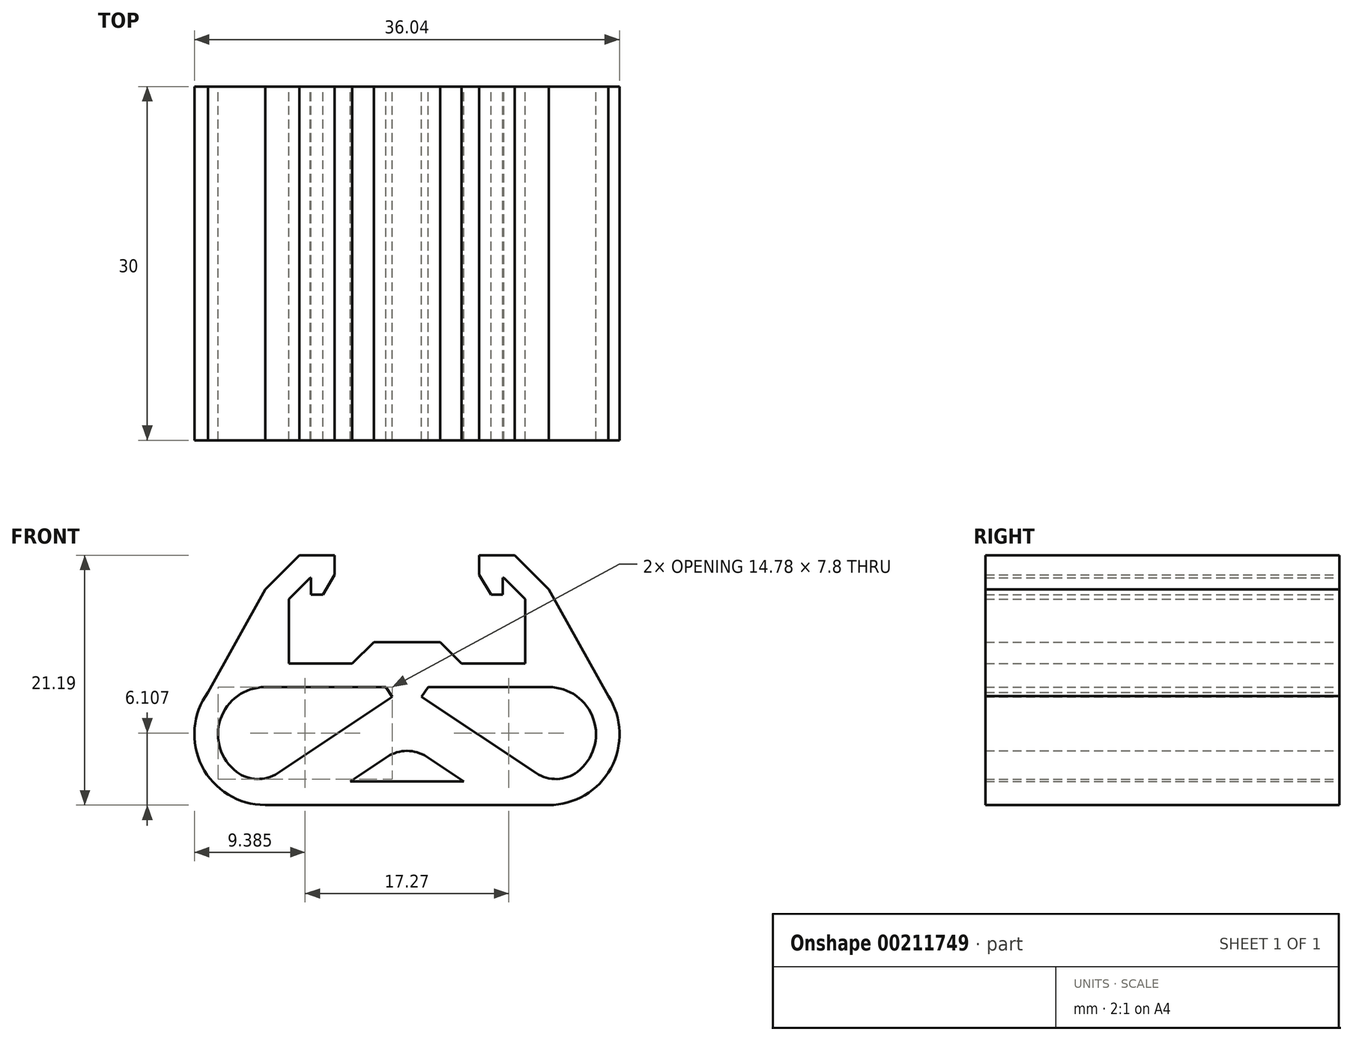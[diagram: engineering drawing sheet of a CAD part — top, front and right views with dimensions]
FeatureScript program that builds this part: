
annotation { "Feature Type Name" : "Feature", "Feature Type Description" : "" }
export const myFeature = defineFeature(function(context is Context, id is Id, definition is map)
    precondition{}
    {
        {
            var Q0;
            Q0=qCreatedBy(makeId("Front.planeOp"),FACE);
            var sketch = newSketch(context, id + "F0", { "sketchPlane" : qUnion([Q0])});
            skLineSegment(sketch, "E0", {"start": v(2.84, -8.2) * mm, "end": v(5.5, -8.2) * mm, "construction": true});
            skLineSegment(sketch, "E1", {"start": v(5.5, -8.2) * mm, "end": v(5.5, -6.56) * mm, "construction": true});
            skLineSegment(sketch, "E2", {"start": v(5.5, -6.56) * mm, "end": v(2.84, -3.9) * mm, "construction": true});
            skLineSegment(sketch, "E3", {"start": v(2.84, -3.9) * mm, "end": v(-2.84, -3.9) * mm, "construction": true});
            skLineSegment(sketch, "E4", {"start": v(-2.84, -3.9) * mm, "end": v(-5.5, -6.56) * mm, "construction": true});
            skLineSegment(sketch, "E5", {"start": v(-5.5, -6.56) * mm, "end": v(-5.5, -8.2) * mm, "construction": true});
            skLineSegment(sketch, "E6", {"start": v(-5.5, -8.2) * mm, "end": v(-2.84, -8.2) * mm, "construction": true});
            skLineSegment(sketch, "E7", {"start": v(-4.64, -10) * mm, "end": v(-10, -10) * mm, "construction": true});
            skLineSegment(sketch, "E8", {"start": v(-10, -10) * mm, "end": v(-10, -4.64) * mm, "construction": true});
            skLineSegment(sketch, "E9", {"start": v(-10, -4.64) * mm, "end": v(-8.2, -2.84) * mm, "construction": true});
            skLineSegment(sketch, "E10", {"start": v(-8.2, -2.84) * mm, "end": v(-8.2, -5.5) * mm, "construction": true});
            skLineSegment(sketch, "E11", {"start": v(-8.2, -5.5) * mm, "end": v(-6.56, -5.5) * mm, "construction": true});
            skLineSegment(sketch, "E12", {"start": v(-6.56, -5.5) * mm, "end": v(-3.9, -2.84) * mm, "construction": true});
            skLineSegment(sketch, "E13", {"start": v(-3.9, -2.84) * mm, "end": v(-3.9, 2.84) * mm, "construction": true});
            skLineSegment(sketch, "E14", {"start": v(-3.9, 2.84) * mm, "end": v(-6.56, 5.5) * mm, "construction": true});
            skLineSegment(sketch, "E15", {"start": v(-6.56, 5.5) * mm, "end": v(-8.2, 5.5) * mm, "construction": true});
            skLineSegment(sketch, "E16", {"start": v(-8.2, 5.5) * mm, "end": v(-8.2, 2.84) * mm, "construction": true});
            skLineSegment(sketch, "E17", {"start": v(-8.2, 2.84) * mm, "end": v(-10, 4.64) * mm, "construction": true});
            skLineSegment(sketch, "E18", {"start": v(-10, 4.64) * mm, "end": v(-10, 10) * mm, "construction": true});
            skLineSegment(sketch, "E19", {"start": v(-10, 10) * mm, "end": v(-4.64, 10) * mm, "construction": true});
            skLineSegment(sketch, "E20", {"start": v(-4.64, 10) * mm, "end": v(-2.84, 8.2) * mm, "construction": true});
            skLineSegment(sketch, "E21", {"start": v(-2.84, 8.2) * mm, "end": v(-5.5, 8.2) * mm, "construction": true});
            skLineSegment(sketch, "E22", {"start": v(-5.5, 8.2) * mm, "end": v(-5.5, 6.56) * mm, "construction": true});
            skLineSegment(sketch, "E23", {"start": v(-5.5, 6.56) * mm, "end": v(-2.84, 3.9) * mm, "construction": true});
            skLineSegment(sketch, "E24", {"start": v(-2.84, 3.9) * mm, "end": v(2.84, 3.9) * mm, "construction": true});
            skLineSegment(sketch, "E25", {"start": v(2.84, 3.9) * mm, "end": v(5.5, 6.56) * mm, "construction": true});
            skLineSegment(sketch, "E26", {"start": v(5.5, 6.56) * mm, "end": v(5.5, 8.2) * mm, "construction": true});
            skLineSegment(sketch, "E27", {"start": v(5.5, 8.2) * mm, "end": v(2.84, 8.2) * mm, "construction": true});
            skLineSegment(sketch, "E28", {"start": v(2.84, 8.2) * mm, "end": v(4.64, 10) * mm, "construction": true});
            skLineSegment(sketch, "E29", {"start": v(4.64, 10) * mm, "end": v(10, 10) * mm, "construction": true});
            skLineSegment(sketch, "E30", {"start": v(10, 10) * mm, "end": v(10, 4.64) * mm, "construction": true});
            skLineSegment(sketch, "E31", {"start": v(10, 4.64) * mm, "end": v(8.2, 2.84) * mm, "construction": true});
            skLineSegment(sketch, "E32", {"start": v(8.2, 2.84) * mm, "end": v(8.2, 5.5) * mm, "construction": true});
            skLineSegment(sketch, "E33", {"start": v(8.2, 5.5) * mm, "end": v(6.56, 5.5) * mm, "construction": true});
            skLineSegment(sketch, "E34", {"start": v(6.56, 5.5) * mm, "end": v(3.9, 2.84) * mm, "construction": true});
            skLineSegment(sketch, "E35", {"start": v(3.9, 2.84) * mm, "end": v(3.9, -2.84) * mm, "construction": true});
            skLineSegment(sketch, "E36", {"start": v(3.9, -2.84) * mm, "end": v(6.56, -5.5) * mm, "construction": true});
            skLineSegment(sketch, "E37", {"start": v(6.56, -5.5) * mm, "end": v(8.2, -5.5) * mm, "construction": true});
            skLineSegment(sketch, "E38", {"start": v(8.2, -5.5) * mm, "end": v(8.2, -2.84) * mm, "construction": true});
            skLineSegment(sketch, "E39", {"start": v(8.2, -2.84) * mm, "end": v(10, -4.64) * mm, "construction": true});
            skLineSegment(sketch, "E40", {"start": v(10, -4.64) * mm, "end": v(10, -10) * mm, "construction": true});
            skLineSegment(sketch, "E41", {"start": v(10, -10) * mm, "end": v(4.64, -10) * mm, "construction": true});
            skLineSegment(sketch, "E42.0", {"start": v(-10.03, -4.56) * mm, "end": v(-10.03, -10.02) * mm});
            skPoint(sketch, "E43.endSnap0", {"position": v(3.9, 0) * mm});
            skLineSegment(sketch, "E44", {"start": v(0, 0) * mm, "end": v(12.85, 0) * mm});
            skLineSegment(sketch, "E45.0", {"start": v(-10.02, -10.03) * mm, "end": v(-4.64, -10.03) * mm});
            skLineSegment(sketch, "E46.0", {"start": v(-6.13, -0.84) * mm, "end": v(-6.13, -2.5) * mm});
            skLineSegment(sketch, "E47", {"start": v(-8.12, -4.17) * mm, "end": v(-7.12, -4.17) * mm});
            skLineSegment(sketch, "E48.trimOffspring", {"start": v(-8.12, -10) * mm, "end": v(-8.12, -10.02) * mm});
            skLineSegment(sketch, "E49.0", {"start": v(-6.13, -0.84) * mm, "end": v(-9.13, -0.84) * mm});
            skLineSegment(sketch, "E50.trimOffspring", {"start": v(-8.12, -2.74) * mm, "end": v(-8.12, -4.17) * mm});
            skPoint(sketch, "E51.orphan", {"position": v(-8.2, -4.17) * mm});
            skLineSegment(sketch, "E52.0", {"start": v(-8.12, -2.74) * mm, "end": v(-8.2, -2.74) * mm});
            skLineSegment(sketch, "E53.0", {"start": v(-12.03, -12.03) * mm, "end": v(-1.8, -12.03) * mm});
            skLineSegment(sketch, "E54", {"start": v(-10.03, -4.56) * mm, "end": v(-8.2, -2.74) * mm});
            skLineSegment(sketch, "E55.0", {"start": v(-12.03, -3.74) * mm, "end": v(-9.13, -0.84) * mm});
            skLineSegment(sketch, "E56", {"start": v(-7.12, -4.17) * mm, "end": v(-6.13, -2.5) * mm});
            skLineSegment(sketch, "E57.MirrorCS", {"start": v(10.03, -4.56) * mm, "end": v(10.03, -10.02) * mm});
            skLineSegment(sketch, "E58.MirrorCS", {"start": v(10.03, -4.56) * mm, "end": v(8.2, -2.74) * mm});
            skLineSegment(sketch, "E59.MirrorCS", {"start": v(8.12, -2.74) * mm, "end": v(8.2, -2.74) * mm});
            skLineSegment(sketch, "E60.MirrorCS", {"start": v(8.12, -2.74) * mm, "end": v(8.12, -4.17) * mm});
            skLineSegment(sketch, "E61.MirrorCS", {"start": v(8.12, -4.17) * mm, "end": v(7.12, -4.17) * mm});
            skLineSegment(sketch, "E62.MirrorCS", {"start": v(7.12, -4.17) * mm, "end": v(6.12, -2.5) * mm});
            skLineSegment(sketch, "E63.MirrorCS", {"start": v(6.13, -0.84) * mm, "end": v(6.13, -2.5) * mm});
            skLineSegment(sketch, "E64.MirrorCS", {"start": v(6.13, -0.84) * mm, "end": v(9.13, -0.84) * mm});
            skLineSegment(sketch, "E65.MirrorCS", {"start": v(12.03, -3.74) * mm, "end": v(9.13, -0.84) * mm});
            skArc(sketch, "E66", {"start": v(12.03, -22.02) * mm, "mid": v(17.3, -18.9) * mm, "end": v(17.07, -12.78) * mm});
            skArc(sketch, "E67.MirrorC", {"start": v(-12.03, -22.02) * mm, "mid": v(-17.38, -18.73) * mm, "end": v(-16.85, -12.46) * mm});
            skArc(sketch, "E68.0", {"start": v(-14.44, -19.22) * mm, "mid": v(-15.82, -14.75) * mm, "end": v(-12.03, -12.02) * mm});
            skArc(sketch, "E69.0", {"start": v(14.44, -19.22) * mm, "mid": v(15.82, -14.75) * mm, "end": v(12.03, -12.02) * mm});
            skLineSegment(sketch, "E70.0", {"start": v(-12.03, -22.03) * mm, "end": v(12.03, -22.03) * mm});
            skLineSegment(sketch, "E71.0", {"start": v(-4.8, -20.03) * mm, "end": v(4.8, -20.03) * mm});
            skPoint(sketch, "E72.orphan", {"position": v(-12.03, -12.03) * mm});
            skPoint(sketch, "E73.orphan", {"position": v(12.03, -12.03) * mm});
            skLineSegment(sketch, "E74", {"start": v(-2.81, -8.2) * mm, "end": v(2.84, -8.2) * mm});
            skLineSegment(sketch, "E75.0", {"start": v(-2.81, -8.2) * mm, "end": v(-4.64, -10.02) * mm});
            skLineSegment(sketch, "E76.MirrorCS", {"start": v(2.81, -8.2) * mm, "end": v(4.64, -10.02) * mm});
            skLineSegment(sketch, "E77.trimOffspring", {"start": v(4.64, -10.03) * mm, "end": v(10.02, -10.03) * mm});
            skLineSegment(sketch, "E78", {"start": v(-12.02, -3.74) * mm, "end": v(-16.85, -12.46) * mm});
            skLineSegment(sketch, "E79", {"start": v(12.03, -3.74) * mm, "end": v(17.07, -12.78) * mm});
            skLineSegment(sketch, "E80", {"start": v(-10.97, -19.32) * mm, "end": v(-1.25, -12.85) * mm});
            skLineSegment(sketch, "E81", {"start": v(1.25, -12.85) * mm, "end": v(10.97, -19.32) * mm});
            skLineSegment(sketch, "E82.0", {"start": v(-4.8, -20.03) * mm, "end": v(-1.66, -17.93) * mm});
            skLineSegment(sketch, "E83.0", {"start": v(1.66, -17.93) * mm, "end": v(4.8, -20.03) * mm});
            skLineSegment(sketch, "E84", {"start": v(-1.8, -12.03) * mm, "end": v(-1.25, -12.85) * mm});
            skLineSegment(sketch, "E85.MirrorCS", {"start": v(1.8, -12.03) * mm, "end": v(1.25, -12.85) * mm});
            skPoint(sketch, "E86.orphan", {"position": v(-0.83, -13.47) * mm});
            skPoint(sketch, "E87.orphan", {"position": v(-2.15, -11.5) * mm});
            skPoint(sketch, "E88.orphan", {"position": v(0.83, -13.47) * mm});
            skPoint(sketch, "E89.orphan", {"position": v(2.15, -11.5) * mm});
            skLineSegment(sketch, "E90.trimOffspring", {"start": v(1.8, -12.03) * mm, "end": v(12.03, -12.03) * mm});
            skPoint(sketch, "E91.orphan", {"position": v(0, -12.03) * mm});
            skPoint(sketch, "E92.visualSharp", {"position": v(-12.03, -20.02) * mm});
            skArc(sketch, "E92.filletArc", {"start": v(-14.44, -19.22) * mm, "mid": v(-12.72, -19.82) * mm, "end": v(-10.97, -19.32) * mm});
            skPoint(sketch, "E93.visualSharp", {"position": v(12.03, -20.02) * mm});
            skArc(sketch, "E93.filletArc", {"start": v(10.97, -19.32) * mm, "mid": v(12.72, -19.82) * mm, "end": v(14.44, -19.22) * mm});
            skPoint(sketch, "E94.visualSharp", {"position": v(0, -16.83) * mm});
            skArc(sketch, "E94.filletArc", {"start": v(1.66, -17.93) * mm, "mid": v(0, -17.43) * mm, "end": v(-1.66, -17.93) * mm});
            skSolve(sketch);
        }
        {
            var Q0;
            {var subQ6=sQuery(id+"F0.wireOp",EDGE,"E42.0");Q0=makeQuery(id+"F0.imprint","IMPRINT",FACE,{"disambiguationData":[TD([[makeQuery(id+"F0.imprint","IMPRINT",EDGE,{"derivedFrom":subQ6}),-1.0]])]});}
            extrude(context, id + "F1", {"entities" : qUnion([Q0]), "depth" : 30 * mm});
        }
    });
